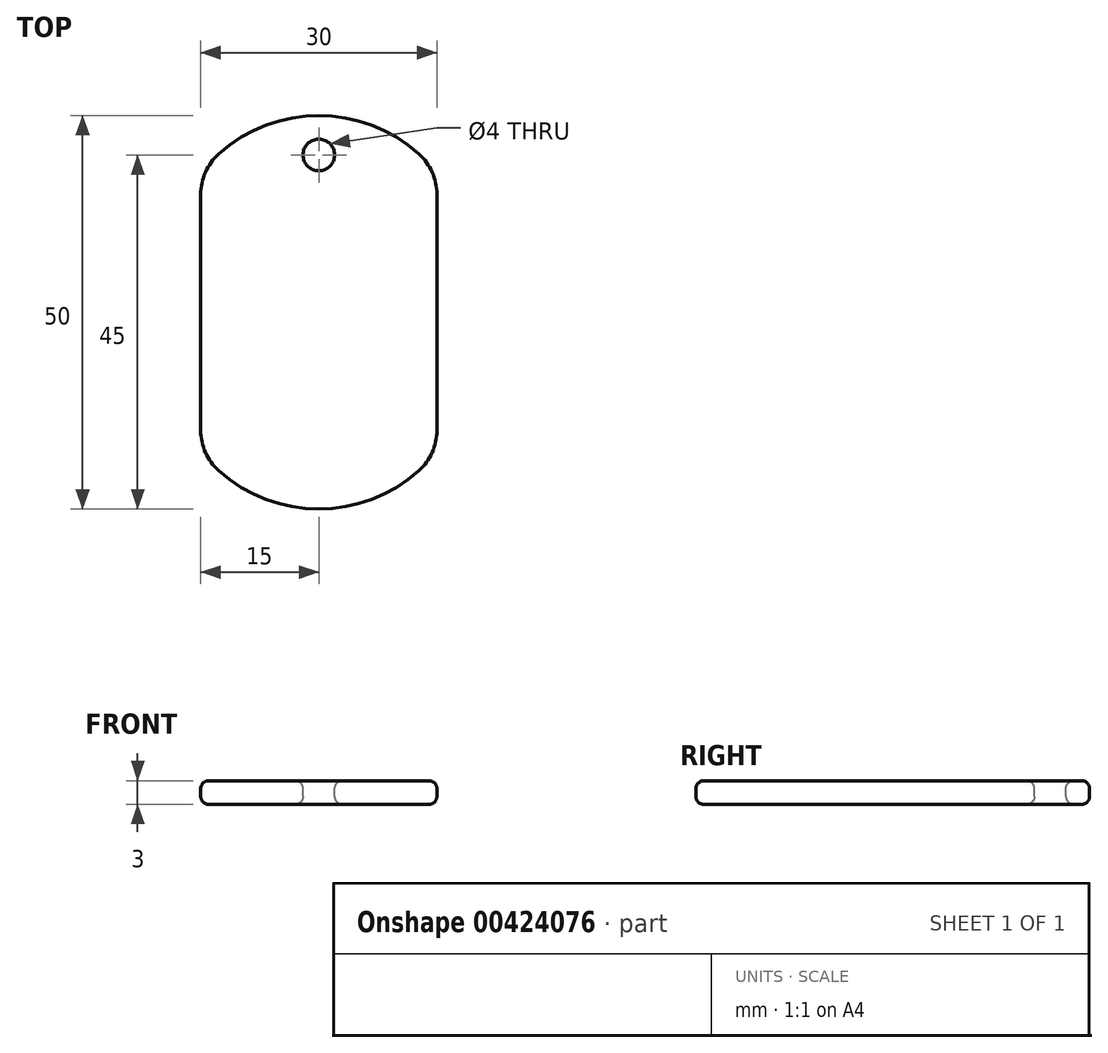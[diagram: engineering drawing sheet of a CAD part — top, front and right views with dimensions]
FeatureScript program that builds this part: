
annotation { "Feature Type Name" : "Feature", "Feature Type Description" : "" }
export const myFeature = defineFeature(function(context is Context, id is Id, definition is map)
    precondition{}
    {
        {
            var Q0;
            Q0=qCreatedBy(makeId("Top.planeOp"),FACE);
            var sketch = newSketch(context, id + "F0", { "sketchPlane" : qUnion([Q0])});
            skLineSegment(sketch, "E0", {"start": v(0, 0) * mm, "end": v(25.46, 0) * mm, "construction": true});
            skLineSegment(sketch, "E1.left", {"start": v(15, 15) * mm, "end": v(15, -15) * mm});
            skLineSegment(sketch, "E1.right", {"start": v(-15, 15) * mm, "end": v(-15, -15) * mm});
            skPoint(sketch, "E1.middle", {"position": v(0, 0) * mm});
            skArc(sketch, "E2", {"start": v(-12.73, 20.1) * mm, "mid": v(0, 25) * mm, "end": v(12.73, 20.1) * mm});
            skArc(sketch, "E3", {"start": v(-15, 15) * mm, "mid": v(-14.4, 17.8) * mm, "end": v(-12.73, 20.1) * mm});
            skArc(sketch, "E4", {"start": v(15, 15) * mm, "mid": v(14.4, 17.8) * mm, "end": v(12.73, 20.1) * mm});
            skPoint(sketch, "E5", {"position": v(0, 25) * mm});
            skArc(sketch, "E6.MirrorCS", {"start": v(-15, -15) * mm, "mid": v(-14.4, -17.8) * mm, "end": v(-12.73, -20.1) * mm});
            skArc(sketch, "E7.MirrorCS", {"start": v(-12.73, -20.1) * mm, "mid": v(0, -25) * mm, "end": v(12.73, -20.1) * mm});
            skArc(sketch, "E8.MirrorCS", {"start": v(15, -15) * mm, "mid": v(14.4, -17.8) * mm, "end": v(12.73, -20.1) * mm});
            skSolve(sketch);
        }
        {
            var Q0;
            Q0=qSketchRegion(id+"F0",true);
            extrude(context, id + "F1", {"entities" : qUnion([Q0]), "depth" : 3 * mm});
        }
        {
            var Q0;
            Q0=makeQuery(id+"F1.opExtrude","CAP_FACE",FACE,{"disambiguationData":[OSD([sQuery(id+"F0.wireOp",EDGE,"E1.left"),sQuery(id+"F0.wireOp",EDGE,"E1.right"),sQuery(id+"F0.wireOp",EDGE,"E2"),sQuery(id+"F0.wireOp",EDGE,"E3"),sQuery(id+"F0.wireOp",EDGE,"E4"),sQuery(id+"F0.wireOp",EDGE,"E6.MirrorCS"),sQuery(id+"F0.wireOp",EDGE,"E7.MirrorCS"),sQuery(id+"F0.wireOp",EDGE,"E8.MirrorCS")])],"isStart":false});
            var sketch = newSketch(context, id + "F2", { "sketchPlane" : qUnion([Q0])});
            skPoint(sketch, "E9", {"position": v(0, 20) * mm});
            skSolve(sketch);
        }
        {
            var Q0;
            Q0=sQuery(id+"F2.wireOp",VERTEX,"E9");
            var Q1;
            Q1=makeQuery(id+"F1.opExtrude","SWEPT_BODY",BODY,{"disambiguationData":[OSD([sQuery(id+"F0.wireOp",EDGE,"E1.left"),sQuery(id+"F0.wireOp",EDGE,"E1.right"),sQuery(id+"F0.wireOp",EDGE,"E2"),sQuery(id+"F0.wireOp",EDGE,"E3"),sQuery(id+"F0.wireOp",EDGE,"E4"),sQuery(id+"F0.wireOp",EDGE,"E6.MirrorCS"),sQuery(id+"F0.wireOp",EDGE,"E7.MirrorCS"),sQuery(id+"F0.wireOp",EDGE,"E8.MirrorCS")])]});
            hole(context, id + "F3", {"style" : HoleStyle.SIMPLE, "endStyle" : HoleEndStyle.THROUGH, "holeDiameter" : 4 * mm, "locations" : qUnion([Q0]), "scope" : qUnion([Q1]), "isTappedThrough" : true});
        }
        {
            var Q0;
            Q0=makeQuery(id+"F1.opExtrude","CAP_FACE",FACE,{"disambiguationData":[OSD([sQuery(id+"F0.wireOp",EDGE,"E1.left"),sQuery(id+"F0.wireOp",EDGE,"E1.right"),sQuery(id+"F0.wireOp",EDGE,"E2"),sQuery(id+"F0.wireOp",EDGE,"E3"),sQuery(id+"F0.wireOp",EDGE,"E4"),sQuery(id+"F0.wireOp",EDGE,"E6.MirrorCS"),sQuery(id+"F0.wireOp",EDGE,"E7.MirrorCS"),sQuery(id+"F0.wireOp",EDGE,"E8.MirrorCS")])],"isStart":false});
            var Q1;
            Q1=makeQuery(id+"F1.opExtrude","CAP_FACE",FACE,{"disambiguationData":[OSD([sQuery(id+"F0.wireOp",EDGE,"E1.left"),sQuery(id+"F0.wireOp",EDGE,"E1.right"),sQuery(id+"F0.wireOp",EDGE,"E2"),sQuery(id+"F0.wireOp",EDGE,"E3"),sQuery(id+"F0.wireOp",EDGE,"E4"),sQuery(id+"F0.wireOp",EDGE,"E6.MirrorCS"),sQuery(id+"F0.wireOp",EDGE,"E7.MirrorCS"),sQuery(id+"F0.wireOp",EDGE,"E8.MirrorCS")])],"isStart":true});
            fillet(context, id + "F4", {"entities" : qUnion([Q0, Q1]), "radius" : 1 * mm, "tangentPropagation" : true, "allowEdgeOverflow" : false});
        }
    });
